# Revit family: QF_MACOM_SAL_GA-NA
name_source: partatom
category: Equipamento especial
units: mm (PartAtom-declared; Revit-internal decimal feet)

## family parameters
Com base no plano de trabalho = Não
Compartilhado = Não
Corte com vazios quando carregada = Não
Cota do conector redondo = Utilizar diâmetro
Número OmniClass = 23.40.40.14.17.11
Ponto de cálculo do ambiente = Não
Sempre na vertical = Sim
Tipo de parte = Normal
Título OmniClass = Cookers, Ovens, Stoves

## types (2) — shared parameters
Capacity = 01 GN 1/1
Depth = 425,000 mm
Descrição = SALAMANDRA A GAS MACOM
Elevação padrão = 0,000 mm
Fabricante = MACOM
Gas Connection Height = 0,000 mm
Gas Consumption GN = 0 m³/h
Gas Size = 3/4"
Height = 439,000 mm
Show Logo = Sim
URL = https://www.acosmacom.com.br
Volume = 0,13 m³
Weight = 26,70 kg
Width = 711,000 mm

## per-type parameters (varying)
| type | Gas Consumption GLP | Gas Input GLP | Gas Input GN | Gas Pressure |
| SAL-GA | 0,31 Kg/h | 14285 Btu/h |  | 0,03 bar |
| SAL-NA |  | 0 Btu/h | 3600 Kcal/h | 0,02 bar |

note: column(s) folded — value = type name in every type: Modelo

## geometry (parser evidence)
native form markers: Sweep x11
no freeform markers — native parametric forms only
